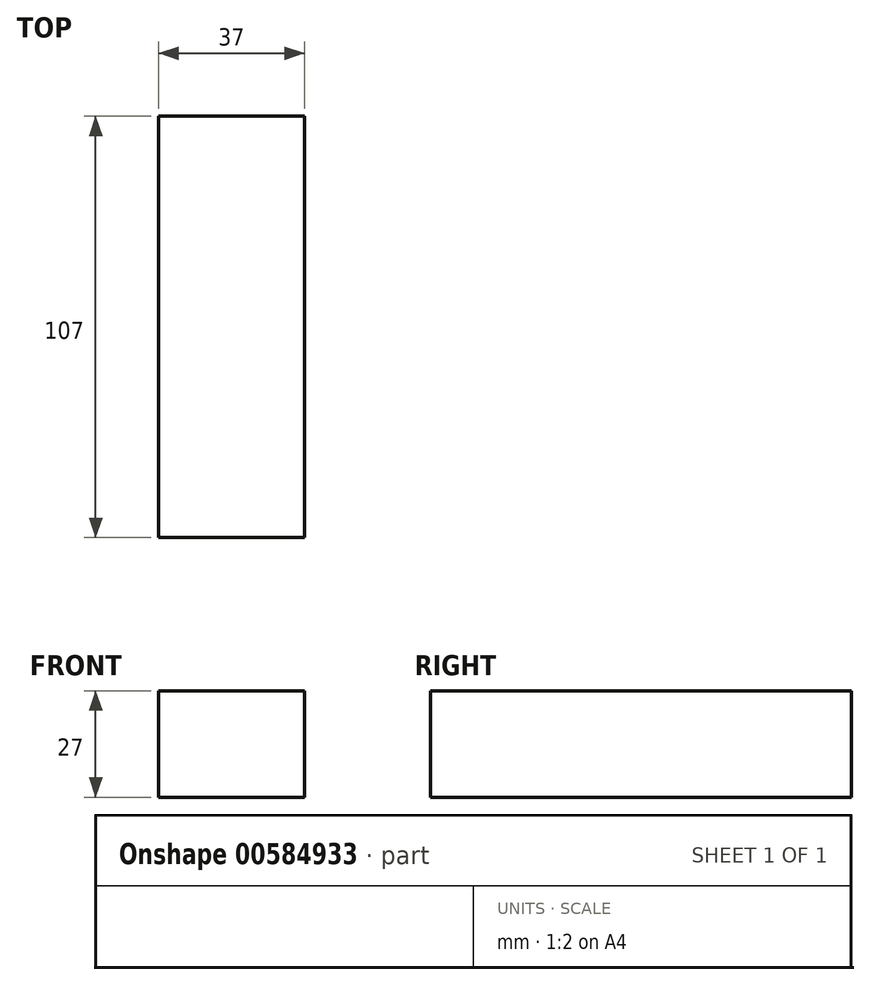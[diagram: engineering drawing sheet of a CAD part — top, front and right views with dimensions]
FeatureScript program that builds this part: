
annotation { "Feature Type Name" : "Feature", "Feature Type Description" : "" }
export const myFeature = defineFeature(function(context is Context, id is Id, definition is map)
    precondition{}
    {
        {
            var Q0;
            Q0=qCreatedBy(makeId("Right.planeOp"),FACE);
            var sketch = newSketch(context, id + "F0", { "sketchPlane" : qUnion([Q0])});
            skLineSegment(sketch, "E0.bottom", {"start": v(53.5, -13.5) * mm, "end": v(-53.5, -13.5) * mm});
            skLineSegment(sketch, "E0.top", {"start": v(53.5, 13.5) * mm, "end": v(-53.5, 13.5) * mm});
            skLineSegment(sketch, "E0.left", {"start": v(53.5, -13.5) * mm, "end": v(53.5, 13.5) * mm});
            skLineSegment(sketch, "E0.right", {"start": v(-53.5, -13.5) * mm, "end": v(-53.5, 13.5) * mm});
            skPoint(sketch, "E0.middle", {"position": v(0, 0) * mm});
            skArc(sketch, "E1", {"start": v(40, -13.5) * mm, "mid": v(53.5, 0) * mm, "end": v(40, 13.5) * mm, "construction": true});
            skSolve(sketch);
        }
        {
            var Q0;
            Q0=makeQuery(id+"F0.imprint","IMPRINT",FACE,{"disambiguationData":[TD([[makeQuery(id+"F0.imprint","IMPRINT",EDGE,{"derivedFrom":sQuery(id+"F0.wireOp",EDGE,"E0.bottom")}),-1.0]])]});
            extrude(context, id + "F1", {"entities" : qUnion([Q0]), "depth" : 37 * mm, "offsetDistance" : 25 * mm, "symmetric" : true});
        }
    });
